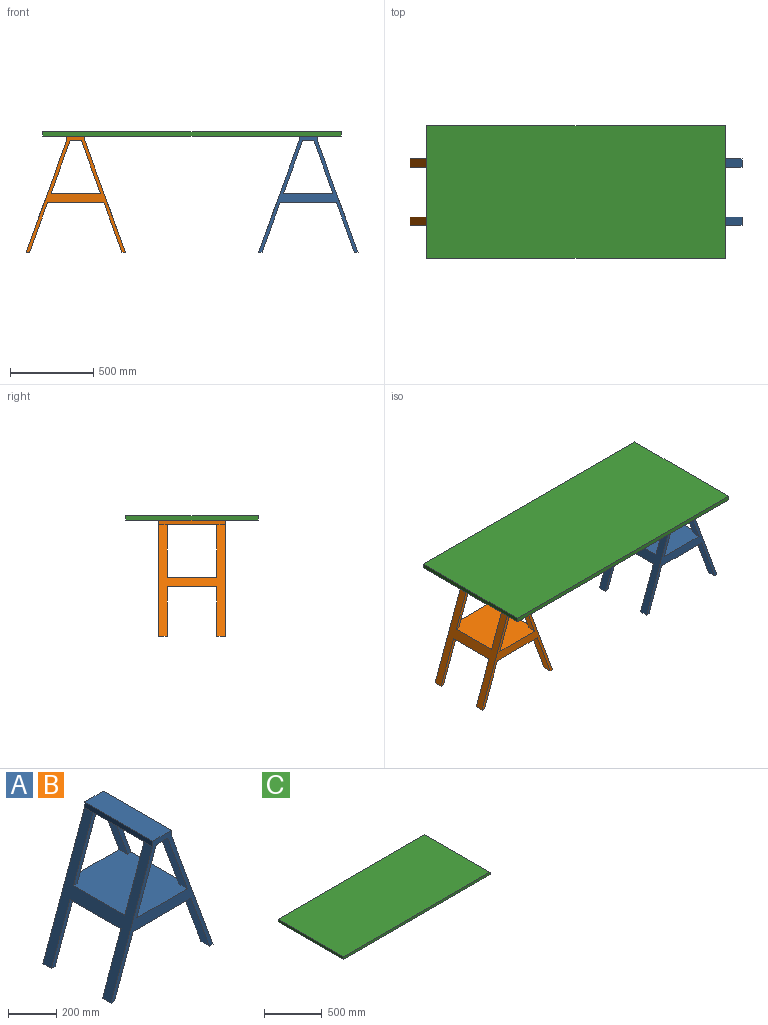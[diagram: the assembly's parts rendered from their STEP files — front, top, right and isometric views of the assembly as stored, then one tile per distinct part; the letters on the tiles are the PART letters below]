
ASSEMBLY  parts=3 mates=2
PART A: 30 faces, bbox 599.2x400x700 mm
  f0: plane 50x21.28mm, normal (0,0,-1), area 1064.2mm2, adj f11,f13,f20,f28
  f1: plane 50x21.28mm, normal (0,0,-1), area 1064.2mm2, adj f3,f17,f21,f24
  f2: plane 314.7x114.54mm, normal (0.94,0,-0.34), area 16744.6mm2, adj f6,f8,f21,f27
  f3: plane 298.17x108.53mm, normal (0.94,0,-0.34), area 15865.4mm2, adj f1,f10,f21,f24
  f4: plane 298.17x108.53mm, normal (-0.94,0,-0.34), area 15865.4mm2, adj f10,f12,f21,f29
  f5: plane 314.7x114.54mm, normal (-0.94,0,-0.34), area 16744.6mm2, adj f6,f8,f21,f22
  f6: plane 400x339.55mm, normal (0,0,1), area 131563mm2, adj f2,f5,f7,f13,f17,f19,f20,f21
  f7: plane 314.7x114.54mm, normal (0.94,0,-0.34), area 16744.6mm2, adj f6,f8,f20,f26
  f8: plane 400x110.47mm, normal (0,0,-1), area 39931.1mm2, adj f2,f5,f7,f14,f16,f19,f20,f21
  f9: plane 298.17x108.53mm, normal (0.94,0,-0.34), area 15865.4mm2, adj f10,f18,f20,f25
  f10: plane 400x382.12mm, normal (0,0,-1), area 148589.8mm2, adj f3,f4,f9,f11,f13,f17,f20,f21
  f11: plane 298.17x108.53mm, normal (-0.94,0,-0.34), area 15865.4mm2, adj f0,f10,f20,f28
  f12: plane 50x21.28mm, normal (0,0,-1), area 1064.2mm2, adj f4,f13,f21,f29
  f13: plane 671.34x400mm, normal (0.94,0,0.34), area 90111.7mm2, adj f0,f6,f10,f12,f14,f20,f21,f22
  f14: plane 400x28.66mm, normal (1,0,0), area 11462.3mm2, adj f8,f13,f15,f20,f21
  f15: plane 400x110.47mm, normal (0,0,1), area 44187.8mm2, adj f14,f16,f20,f21
  f16: plane 400x28.66mm, normal (-1,0,0), area 11462.3mm2, adj f8,f15,f17,f20,f21
  f17: plane 671.34x400mm, normal (-0.94,0,0.34), area 90111.7mm2, adj f1,f6,f10,f16,f18,f20,f21,f24
  f18: plane 50x21.28mm, normal (0,0,-1), area 1064.2mm2, adj f9,f17,f20,f25
  f19: plane 314.7x114.54mm, normal (-0.94,0,-0.34), area 16744.6mm2, adj f6,f8,f20,f23
  f20: plane 700x599.17mm, normal (0,-1,0), area 50353.7mm2, adj f0,f6,f7,f8,f9,f10,f11,f13
  f21: plane 700x599.17mm, normal (0,1,0), area 50353.7mm2, adj f1,f2,f3,f4,f5,f6,f8,f10
  f22: plane 314.7x135.82mm, normal (0,-1,0), area 6697.8mm2, adj f5,f6,f8,f13
  f23: plane 314.7x135.82mm, normal (0,1,0), area 6697.8mm2, adj f6,f8,f13,f19
  f24: plane 298.17x129.81mm, normal (0,-1,0), area 6346.2mm2, adj f1,f3,f10,f17
  f25: plane 298.17x129.81mm, normal (0,1,0), area 6346.2mm2, adj f9,f10,f17,f18
  f26: plane 314.7x135.82mm, normal (0,1,0), area 6697.8mm2, adj f6,f7,f8,f17
  f27: plane 314.7x135.82mm, normal (0,-1,0), area 6697.8mm2, adj f2,f6,f8,f17
  f28: plane 298.17x129.81mm, normal (0,1,0), area 6346.2mm2, adj f0,f10,f11,f13
  f29: plane 298.17x129.81mm, normal (0,-1,0), area 6346.2mm2, adj f4,f10,f12,f13
PART B: same geometry as A
PART C: 6 faces, bbox 1800x800x27 mm
  f0: plane 1800x27mm, normal (0,-1,0), area 48600mm2, adj f1,f3,f4,f5
  f1: plane 800x27mm, normal (1,0,0), area 21600mm2, adj f0,f2,f4,f5
  f2: plane 1800x27mm, normal (0,1,0), area 48600mm2, adj f1,f3,f4,f5
  f3: plane 800x27mm, normal (-1,0,0), area 21600mm2, adj f0,f2,f4,f5
  f4: plane 1800x800mm, normal (0,0,1), area 1440000mm2, adj f0,f1,f2,f3
  f5: plane 1800x800mm, normal (0,0,-1), area 1440000mm2, adj f0,f1,f2,f3
PLACE A t=(714.95,59.39,53.77)mm
PLACE B t=(-685.05,59.39,53.77)mm fixed
PLACE C t=(14.95,59.39,53.77)mm
MATE fastened A.f15 <-> C.f5  axis (0,0,1) through (714.95,59.39,53.77)mm
MATE fastened C.f5 <-> B.f15  axis (0,0,-1) through (-885.05,59.39,53.77)mm
